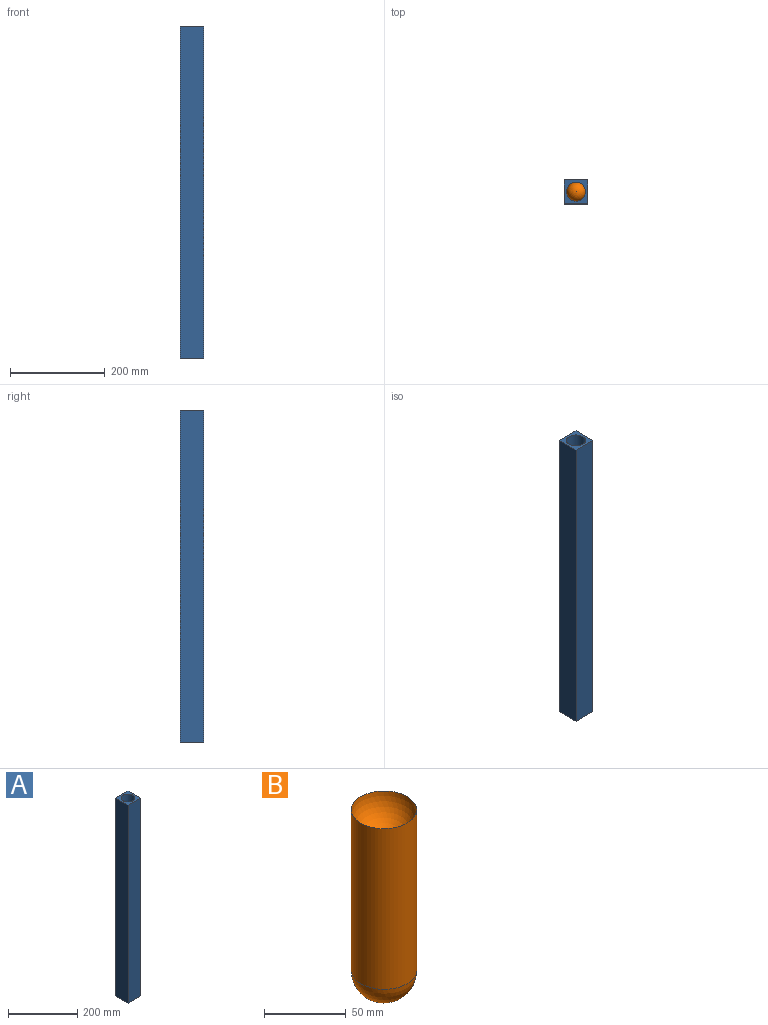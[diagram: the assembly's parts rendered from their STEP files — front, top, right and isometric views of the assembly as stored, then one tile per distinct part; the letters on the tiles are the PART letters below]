
ASSEMBLY  parts=2 mates=1
PART A: 7 faces, bbox 50x50x700 mm
  f0: plane 700x50mm, normal (-1,0,0), area 35000mm2, adj f1,f3,f4,f5
  f1: plane 700x50mm, normal (0,-1,0), area 35000mm2, adj f0,f2,f4,f5
  f2: plane 700x50mm, normal (1,0,0), area 35000mm2, adj f1,f3,f4,f5
  f3: plane 700x50mm, normal (0,1,0), area 35000mm2, adj f0,f2,f4,f5
  f4: plane 50x50mm, normal (0,0,1), area 1243.4mm2, adj f0,f1,f2,f3,f6
  f5: plane 50x50mm, normal (0,0,-1), area 1243.4mm2, adj f0,f1,f2,f3,f6
  f6: cylinder r=20mm len=700mm, axis (0,0,-1), area 87964.6mm2, adj f4,f5
PART B: 3 faces, bbox 40x40x140.5 mm
  f0: sphere r=20.01mm, area 2452mm2, adj f1
  f1: cylinder r=20mm len=120.5mm, axis (0,0,-1), area 15142.5mm2, adj f0,f2
  f2: sphere r=20mm, area 2513.3mm2, adj f1
PLACE A t=(-328.88,-267.55,-255.16)mm fixed
PLACE B rot(axis=(0.29,-0.96,0),180deg) t=(-272.8,-267.75,181.43)mm
MATE cylindrical B.f1 <-> A.f6  axis (0,0,1) through (-272.8,-267.75,121.18)mm
